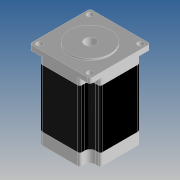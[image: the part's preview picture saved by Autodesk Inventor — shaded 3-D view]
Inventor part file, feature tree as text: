
AUTODESK INVENTOR PART (.ipt)
format: ipt  version: 2017 (Build 210142000, 142)  size: 248,832 bytes
history: native  units: mm
features: other x5, extrude x3, sketch x3, plane x2, split x2, fillet x1
ambient origin geometry x8: Origin, YZ Plane, XZ Plane, XY Plane, X Axis, Y Axis, Z Axis, Center Point
bodies: Body1 (feature_tree), Body2 (feature_tree), Body3 (feature_tree)
feature tree (16):
  other  "Sólido1"
  extrude  "Extrusión1"  Depth=2.0mm
  extrude  "Extrusión2"  Depth=61.0mm
  extrude  "Extrusión3"  Depth=4.7mm TaperAngle=0.0deg
  fillet  "Empalme1"  Radius=37.0mm
  plane  "Plano de trabajo1"
  plane  "Plano de trabajo2"
  split  "Dividir1"
  split  "Dividir2"
  sketch  "Boceto1"  dims[d0=56.0mm d1=2.0mm]
  sketch  "Boceto2"  dims[d2=5.3mm d3=61.0mm]
  sketch  "Boceto3"  dims[d4=10.0mm d5=4.7mm d6=0.0mm d7=37.0mm d8=71.3mm d9=0.0mm d10=38.0mm d11=1.6mm d12=0.0mm d13=-11.0mm d14=-11.0mm d15=2.0mm]
  other  "Sólido2"
  other  "Sólido3"
  other  "Sólido4"
  other  "Sólido5"
